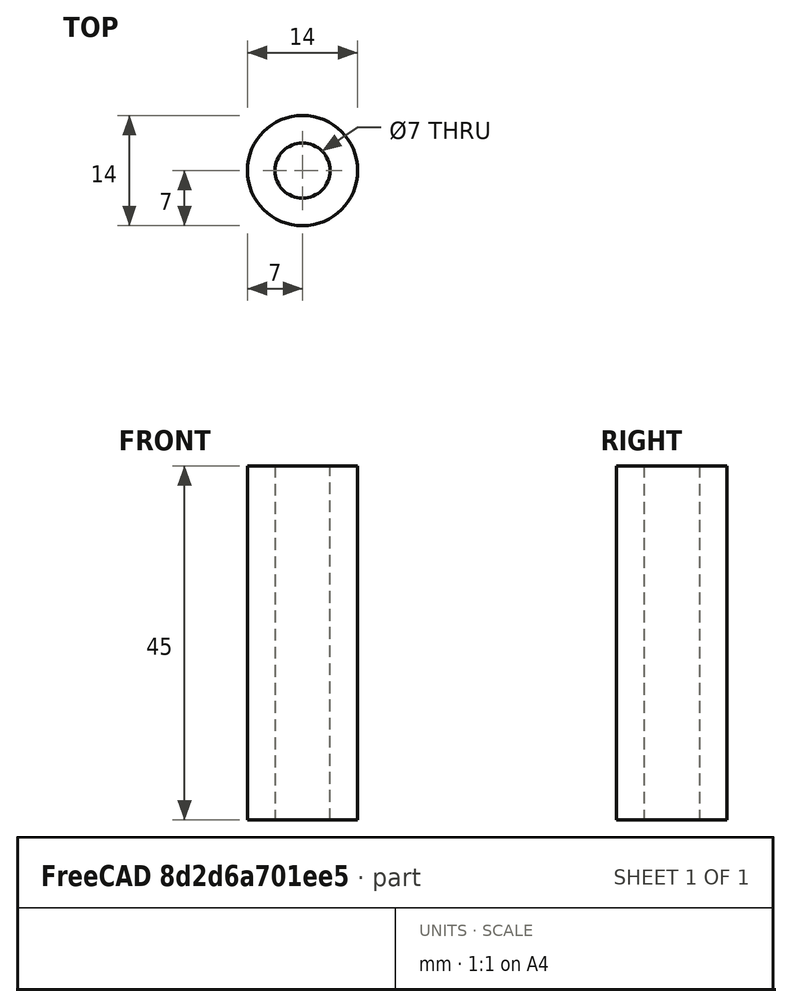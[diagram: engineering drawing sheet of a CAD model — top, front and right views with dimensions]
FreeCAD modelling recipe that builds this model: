
FCSTD DOCUMENT  (FreeCAD 2024.2R37179 (Git))
Label: 45mm
License: All rights reserved
LicenseURL: https://en.wikipedia.org/wiki/All_rights_reserved
objects: Sketcher::SketchObject×1, PartDesign::Pad×1, PartDesign::Body×1
note: 4 computed .brp shape members not serialized (recipe doc carries the construction recipe); baked Part::Feature solids carry a one-line shape summary decoded from their .brp

FEATURE [Sketcher::SketchObject] Sketch
  AttachmentSupport = -> [XY_Plane]
  FullyConstrained = true
  MapMode = 5
  sketch-geometry (2):
    g0: Circle CenterX=0 CenterY=0 CenterZ=0 NormalX=0 NormalY=0 NormalZ=1 AngleXU=0 Radius=3.5
    g1: Circle CenterX=0 CenterY=0 CenterZ=0 NormalX=0 NormalY=0 NormalZ=1 AngleXU=0 Radius=7
  constraints (4):
    c: Coincident(g0,g-1)
    c: Diameter(g0) = 7
    c: Coincident(g1,g0)
    c: Diameter(g1) = 14
FEATURE [PartDesign::Pad] Pad
  Direction = (0,0,1)
  Length = 45
  Length2 = 10
  Profile = -> Sketch
  ReferenceAxis = -> Sketch [N_Axis]
  Refine = true
  Suppressed = false
  Type = 0
  expr: Length = 45
FEATURE [PartDesign::Body] Body
  Group = -> [Sketch,Pad]
  Origin = -> Origin
  Tip = -> Pad
